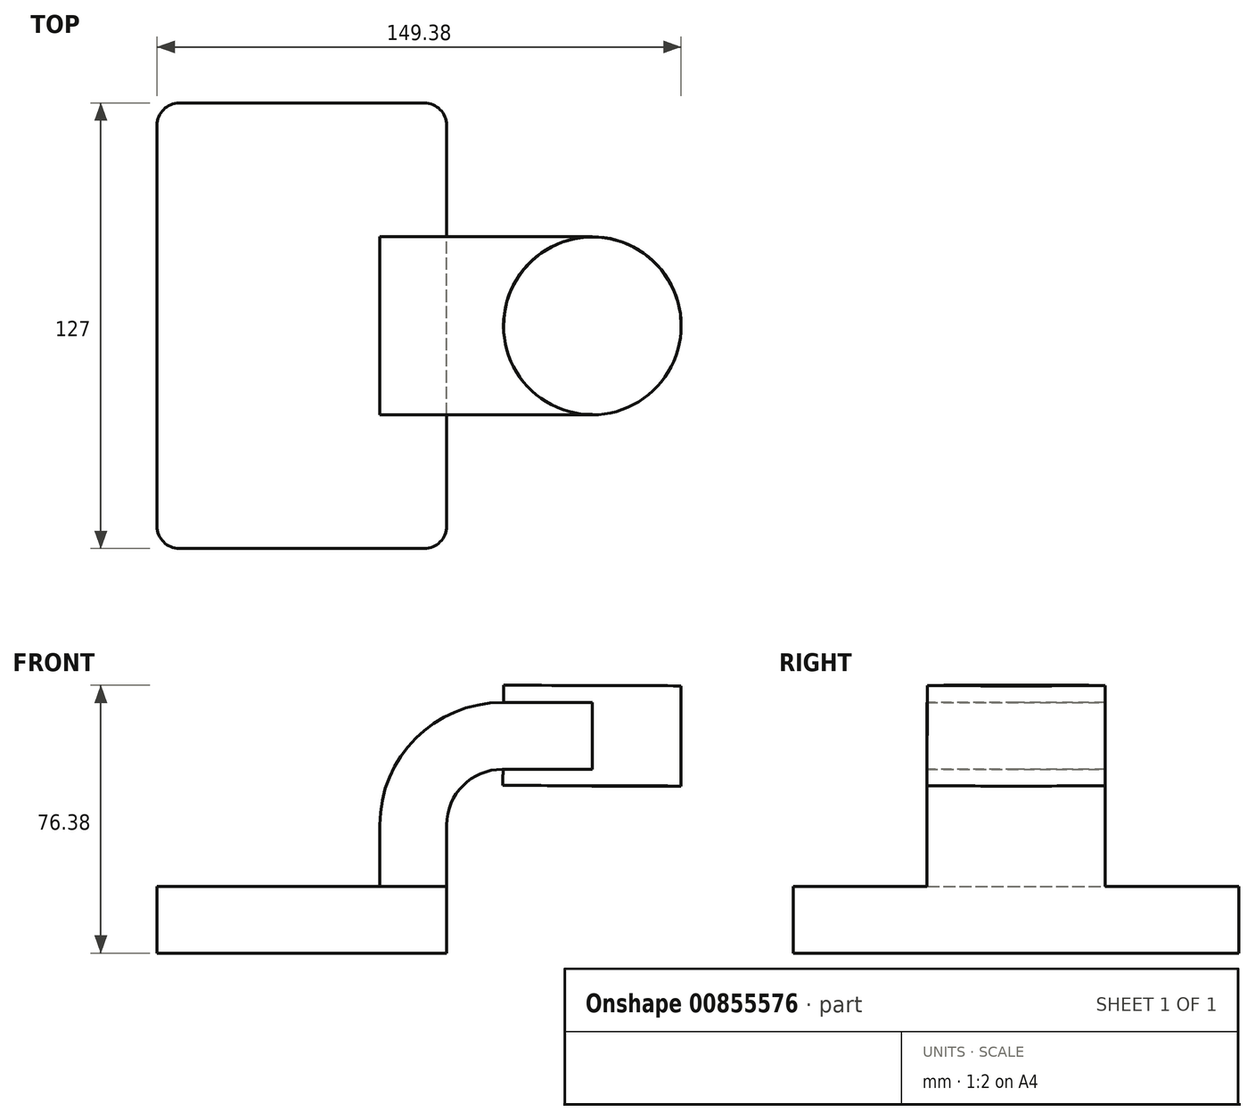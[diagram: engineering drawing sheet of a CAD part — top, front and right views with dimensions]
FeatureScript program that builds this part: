
annotation { "Feature Type Name" : "Feature", "Feature Type Description" : "" }
export const myFeature = defineFeature(function(context is Context, id is Id, definition is map)
    precondition{}
    {
        {
            var Q0;
            Q0=qCreatedBy(makeId("Front.planeOp"),FACE);
            var sketch = newSketch(context, id + "F0", { "sketchPlane" : qUnion([Q0])});
            skLineSegment(sketch, "E0.bottom", {"start": v(41.28, -9.52) * mm, "end": v(-41.28, -9.53) * mm});
            skLineSegment(sketch, "E0.top", {"start": v(41.28, 9.53) * mm, "end": v(-41.28, 9.53) * mm});
            skLineSegment(sketch, "E0.left", {"start": v(41.28, -9.52) * mm, "end": v(41.28, 9.53) * mm});
            skLineSegment(sketch, "E0.right", {"start": v(-41.28, -9.53) * mm, "end": v(-41.28, 9.53) * mm});
            skPoint(sketch, "E0.middle", {"position": v(0, 0) * mm});
            skLineSegment(sketch, "E1", {"start": v(41.28, 9.53) * mm, "end": v(41.28, 27) * mm});
            skLineSegment(sketch, "E2.bottom", {"start": v(108.11, 38.1) * mm, "end": v(57.31, 38.1) * mm});
            skLineSegment(sketch, "E2.top", {"start": v(108.11, 66.68) * mm, "end": v(57.31, 66.68) * mm});
            skLineSegment(sketch, "E2.left", {"start": v(108.11, 38.1) * mm, "end": v(108.11, 66.68) * mm});
            skLineSegment(sketch, "E2.right", {"start": v(57.31, 38.1) * mm, "end": v(57.31, 66.68) * mm});
            skPoint(sketch, "E2.middle", {"position": v(82.71, 52.39) * mm});
            skArc(sketch, "E3", {"start": v(41.27, 27) * mm, "mid": v(45.92, 38.23) * mm, "end": v(57.15, 42.88) * mm});
            skLineSegment(sketch, "E4", {"start": v(57.15, 42.88) * mm, "end": v(82.81, 42.88) * mm});
            skLineSegment(sketch, "E5.0", {"start": v(57.15, 61.93) * mm, "end": v(82.81, 61.93) * mm});
            skArc(sketch, "E5.1", {"start": v(22.22, 27) * mm, "mid": v(32.45, 51.7) * mm, "end": v(57.15, 61.93) * mm});
            skLineSegment(sketch, "E5.2", {"start": v(22.23, 9.53) * mm, "end": v(22.23, 27) * mm});
            skLineSegment(sketch, "E6", {"start": v(82.71, 38.1) * mm, "end": v(82.81, 66.68) * mm});
            skFitSpline(sketch, "E7", {"points": [v(-41.28, 9.53) * mm, v(57.15, 61.93) * mm], "startDerivative": vector(77.5, 102.09) * mm, "endDerivative": vector(111.66, -2.66) * mm});
            skSolve(sketch);
        }
        {
            var Q0;
            Q0=makeQuery(id+"F0.imprint","IMPRINT",FACE,{"disambiguationData":[TD([[makeQuery(id+"F0.imprint","IMPRINT",EDGE,{"derivedFrom":sQuery(id+"F0.wireOp",EDGE,"E0.bottom")}),-1.0]])]});
            extrude(context, id + "F1", {"entities" : qUnion([Q0]), "endBound" : BoundingType.SYMMETRIC, "depth" : 127 * mm, "offsetDistance" : 25.4 * mm});
        }
        {
            var Q0;
            {var subQ6=sQuery(id+"F0.wireOp",EDGE,"E1");Q0=makeQuery(id+"F0.imprint","IMPRINT",FACE,{"disambiguationData":[TD([[makeQuery(id+"F0.imprint","IMPRINT",EDGE,{"derivedFrom":subQ6}),1.0]])]});}
            var Q1;
            {var subQ0=sQuery(id+"F0.wireOp",EDGE,"E4");var subQ1=sQuery(id+"F0.wireOp",EDGE,"E2.right");var subQ2=makeQuery(id+"F0.imprint","INTERSECT",VERTEX,{"derivedFrom":[subQ1,subQ0]});Q1=makeQuery(id+"F0.imprint","IMPRINT",FACE,{"disambiguationData":[TD([[makeQuery(id+"F0.imprint","IMPRINT",EDGE,{"disambiguationData":[TD([[subQ2,-1.0]])],"derivedFrom":subQ1}),-1.0]])]});}
            extrude(context, id + "F2", {"entities" : qUnion([Q0, Q1]), "operationType" : NewBodyOperationType.ADD, "endBound" : BoundingType.SYMMETRIC, "depth" : 50.8 * mm, "offsetDistance" : 25.4 * mm});
        }
        {
            var Q0;
            Q0=makeQuery(id+"F0.imprint","IMPRINT",FACE,{"disambiguationData":[TD([[makeQuery(id+"F0.imprint","IMPRINT",EDGE,{"derivedFrom":sQuery(id+"F0.wireOp",EDGE,"E5.1")}),1.0]])]});
            extrude(context, id + "F3", {"entities" : qUnion([Q0]), "operationType" : NewBodyOperationType.ADD, "endBound" : BoundingType.SYMMETRIC, "depth" : 15.88 * mm, "offsetDistance" : 25.4 * mm});
        }
        {
            var Q0;
            {var subQ0=sQuery(id+"F0.wireOp",EDGE,"E2.left");Q0=makeQuery(id+"F0.imprint","IMPRINT",FACE,{"disambiguationData":[TD([[makeQuery(id+"F0.imprint","IMPRINT",EDGE,{"derivedFrom":subQ0}),1.0]])]});}
            var Q1;
            Q1=sQuery(id+"F0.wireOp",EDGE,"E6");
            revolve(context, id + "F4", {"operationType" : NewBodyOperationType.ADD, "surfaceOperationType" : NewSurfaceOperationType.NEW, "entities" : qUnion([Q0]), "axis" : qUnion([Q1]), "revolveType" : RevolveType.FULL});
        }
        {
            var Q0;
            Q0=makeQuery(id+"F1.opExtrude","CAP_EDGE",EDGE,{"disambiguationData":[OSD([sQuery(id+"F0.wireOp",EDGE,"E0.left")])],"isStart":false});
            var Q1;
            Q1=makeQuery(id+"F1.opExtrude","CAP_EDGE",EDGE,{"disambiguationData":[OSD([sQuery(id+"F0.wireOp",EDGE,"E0.right")])],"isStart":false});
            var Q2;
            Q2=makeQuery(id+"F1.opExtrude","CAP_EDGE",EDGE,{"disambiguationData":[OSD([sQuery(id+"F0.wireOp",EDGE,"E0.left")])],"isStart":true});
            var Q3;
            Q3=makeQuery(id+"F1.opExtrude","CAP_EDGE",EDGE,{"disambiguationData":[OSD([sQuery(id+"F0.wireOp",EDGE,"E0.right")])],"isStart":true});
            fillet(context, id + "F5", {"entities" : qUnion([Q0, Q1, Q2, Q3]), "radius" : 6.35 * mm, "tangentPropagation" : true, "allowEdgeOverflow" : false});
        }
    });
